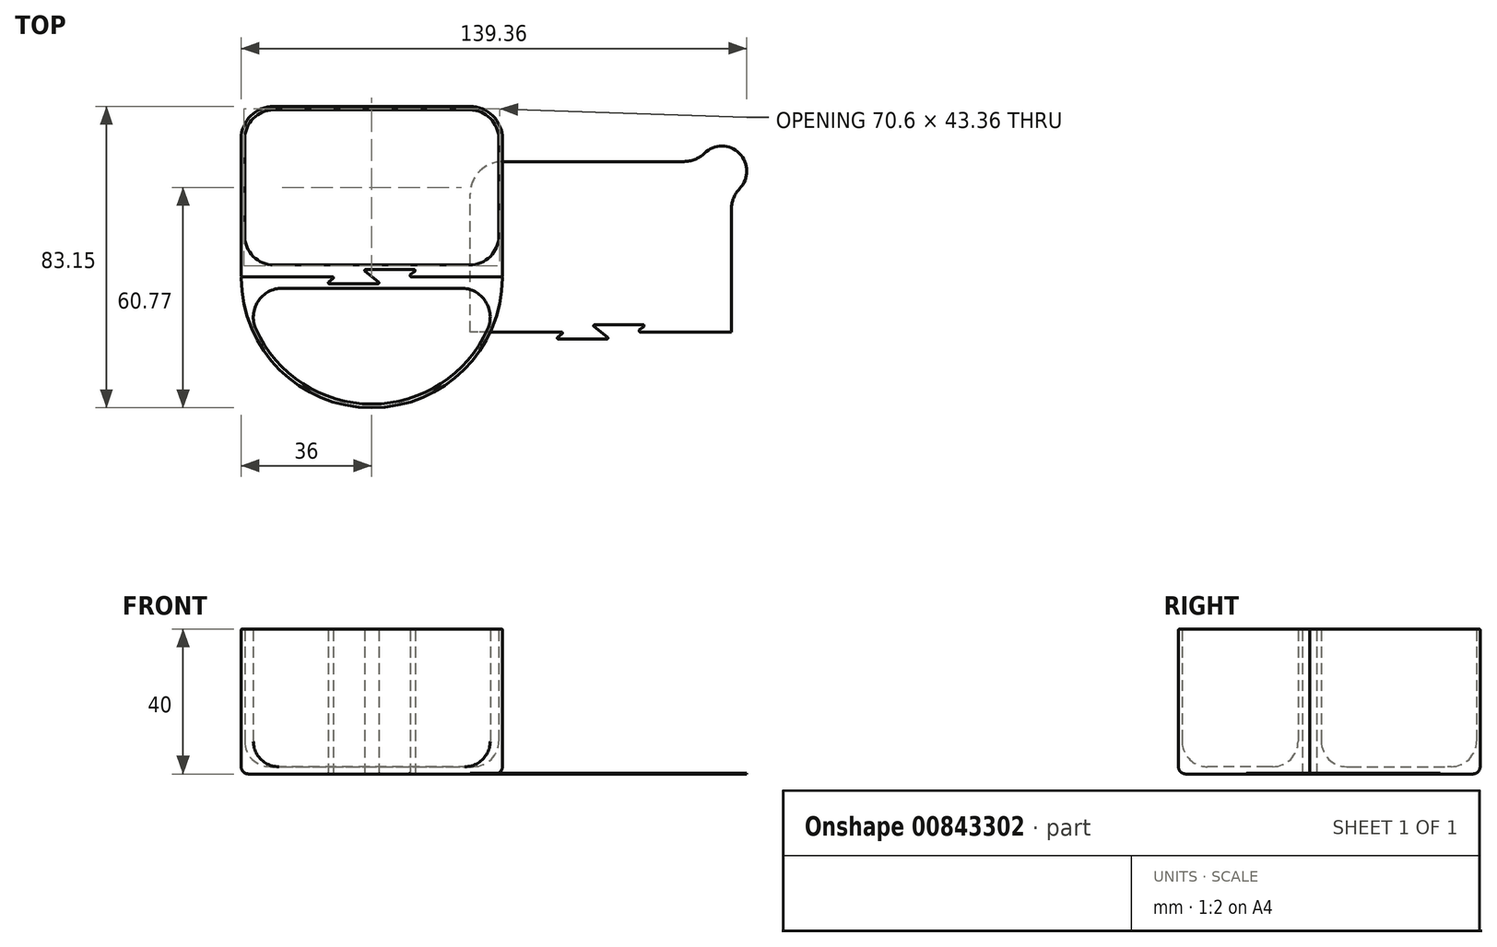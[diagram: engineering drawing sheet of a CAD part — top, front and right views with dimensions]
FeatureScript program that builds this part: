
annotation { "Feature Type Name" : "Feature", "Feature Type Description" : "" }
export const myFeature = defineFeature(function(context is Context, id is Id, definition is map)
    precondition{}
    {
        {
            var Q0;
            Q0=qCreatedBy(makeId("Top.planeOp"),FACE);
            var sketch = newSketch(context, id + "F0", { "sketchPlane" : qUnion([Q0])});
            skLineSegment(sketch, "E0.top", {"start": v(27, 22.5) * mm, "end": v(-27, 22.5) * mm});
            skLineSegment(sketch, "E0.left", {"start": v(35, -12.26) * mm, "end": v(35, 14.5) * mm});
            skLineSegment(sketch, "E0.right", {"start": v(-35, -12.26) * mm, "end": v(-35, 14.5) * mm});
            skPoint(sketch, "E0.middle", {"position": v(0, 0) * mm});
            skPoint(sketch, "E1.visualSharp", {"position": v(-35, 22.5) * mm});
            skArc(sketch, "E1.filletArc", {"start": v(-27, 22.5) * mm, "mid": v(-32.66, 20.16) * mm, "end": v(-35, 14.5) * mm});
            skPoint(sketch, "E2.visualSharp", {"position": v(35, 22.5) * mm});
            skArc(sketch, "E2.filletArc", {"start": v(35, 14.5) * mm, "mid": v(32.66, 20.16) * mm, "end": v(27, 22.5) * mm});
            skArc(sketch, "E3.0", {"start": v(36, 14.5) * mm, "mid": v(33.36, 20.86) * mm, "end": v(27, 23.5) * mm});
            skArc(sketch, "E3.1", {"start": v(-27, 23.5) * mm, "mid": v(-33.36, 20.86) * mm, "end": v(-36, 14.5) * mm});
            skLineSegment(sketch, "E3.2", {"start": v(-36, -23.5) * mm, "end": v(-36, 14.5) * mm});
            skLineSegment(sketch, "E3.3", {"start": v(27, 23.5) * mm, "end": v(-27, 23.5) * mm});
            skLineSegment(sketch, "E3.4", {"start": v(36, -23.5) * mm, "end": v(10.86, -23.5) * mm});
            skLineSegment(sketch, "E3.5", {"start": v(36, -23.5) * mm, "end": v(36, 14.5) * mm});
            skLineSegment(sketch, "E4", {"start": v(1.83, -24.97) * mm, "end": v(-1.83, -22.03) * mm});
            skLineSegment(sketch, "E5", {"start": v(1.64, -25.5) * mm, "end": v(-11.65, -25.5) * mm});
            skLineSegment(sketch, "E6", {"start": v(-11.83, -24.97) * mm, "end": v(-10.67, -24.03) * mm});
            skLineSegment(sketch, "E7", {"start": v(-1.64, -21.5) * mm, "end": v(11.64, -21.5) * mm});
            skLineSegment(sketch, "E8", {"start": v(11.83, -22.03) * mm, "end": v(10.67, -22.97) * mm});
            skLineSegment(sketch, "E9.trimOffspring", {"start": v(-10.86, -23.5) * mm, "end": v(-36, -23.5) * mm});
            skLineSegment(sketch, "E10", {"start": v(-27, -20.26) * mm, "end": v(27, -20.26) * mm});
            skPoint(sketch, "E11.visualSharp", {"position": v(-35, -20.26) * mm});
            skArc(sketch, "E11.filletArc", {"start": v(-35, -12.26) * mm, "mid": v(-32.66, -17.92) * mm, "end": v(-27, -20.26) * mm});
            skPoint(sketch, "E12.visualSharp", {"position": v(35, -20.26) * mm});
            skArc(sketch, "E12.filletArc", {"start": v(27, -20.26) * mm, "mid": v(32.66, -17.92) * mm, "end": v(35, -12.26) * mm});
            skPoint(sketch, "E13.visualSharp", {"position": v(-12.5, -25.5) * mm});
            skArc(sketch, "E13.filletArc", {"start": v(-11.83, -24.97) * mm, "mid": v(-11.93, -25.3) * mm, "end": v(-11.65, -25.5) * mm});
            skPoint(sketch, "E14.visualSharp", {"position": v(-10, -23.5) * mm});
            skArc(sketch, "E14.filletArc", {"start": v(-10.67, -24.03) * mm, "mid": v(-10.57, -23.7) * mm, "end": v(-10.86, -23.5) * mm});
            skPoint(sketch, "E15.visualSharp", {"position": v(2.5, -25.5) * mm});
            skArc(sketch, "E15.filletArc", {"start": v(1.64, -25.5) * mm, "mid": v(1.93, -25.3) * mm, "end": v(1.83, -24.97) * mm});
            skPoint(sketch, "E16.visualSharp", {"position": v(-2.5, -21.5) * mm});
            skArc(sketch, "E16.filletArc", {"start": v(-1.64, -21.5) * mm, "mid": v(-1.93, -21.7) * mm, "end": v(-1.83, -22.03) * mm});
            skPoint(sketch, "E17.visualSharp", {"position": v(12.5, -21.5) * mm});
            skArc(sketch, "E17.filletArc", {"start": v(11.83, -22.03) * mm, "mid": v(11.93, -21.7) * mm, "end": v(11.64, -21.5) * mm});
            skPoint(sketch, "E18.visualSharp", {"position": v(10, -23.5) * mm});
            skArc(sketch, "E18.filletArc", {"start": v(10.67, -22.97) * mm, "mid": v(10.57, -23.3) * mm, "end": v(10.86, -23.5) * mm});
            skSolve(sketch);
        }
        {
            var Q0;
            Q0=makeQuery(id+"F0.imprint","IMPRINT",FACE,{"disambiguationData":[TD([[makeQuery(id+"F0.imprint","IMPRINT",EDGE,{"derivedFrom":sQuery(id+"F0.wireOp",EDGE,"E0.top")}),-1.0]])]});
            extrude(context, id + "F1", {"entities" : qUnion([Q0]), "depth" : 40 * mm, "offsetDistance" : 25 * mm});
        }
        {
            var Q0;
            Q0=makeQuery(id+"F1.opExtrude","CAP_FACE",FACE,{"disambiguationData":[OSD([sQuery(id+"F0.wireOp",EDGE,"E0.top"),sQuery(id+"F0.wireOp",EDGE,"E0.left"),sQuery(id+"F0.wireOp",EDGE,"E0.right"),sQuery(id+"F0.wireOp",EDGE,"E1.filletArc"),sQuery(id+"F0.wireOp",EDGE,"E2.filletArc"),sQuery(id+"F0.wireOp",EDGE,"E3.0"),sQuery(id+"F0.wireOp",EDGE,"E3.1"),sQuery(id+"F0.wireOp",EDGE,"E3.2"),sQuery(id+"F0.wireOp",EDGE,"E3.3"),sQuery(id+"F0.wireOp",EDGE,"E3.4"),sQuery(id+"F0.wireOp",EDGE,"E3.5"),sQuery(id+"F0.wireOp",EDGE,"E4"),sQuery(id+"F0.wireOp",EDGE,"E5"),sQuery(id+"F0.wireOp",EDGE,"E6"),sQuery(id+"F0.wireOp",EDGE,"E7"),sQuery(id+"F0.wireOp",EDGE,"E8"),sQuery(id+"F0.wireOp",EDGE,"E9.trimOffspring"),sQuery(id+"F0.wireOp",EDGE,"E10"),sQuery(id+"F0.wireOp",EDGE,"E11.filletArc"),sQuery(id+"F0.wireOp",EDGE,"E12.filletArc")])],"isStart":true});
            var sketch = newSketch(context, id + "F2", { "sketchPlane" : qUnion([Q0])});
            skArc(sketch, "E19.0", {"start": v(-35, 12.26) * mm, "mid": v(-32.66, 17.92) * mm, "end": v(-27, 20.26) * mm});
            skLineSegment(sketch, "E19.1", {"start": v(-27, 20.26) * mm, "end": v(27, 20.26) * mm});
            skArc(sketch, "E19.2", {"start": v(27, 20.26) * mm, "mid": v(32.66, 17.92) * mm, "end": v(35, 12.26) * mm});
            skLineSegment(sketch, "E19.3", {"start": v(35, 12.26) * mm, "end": v(35, -14.5) * mm});
            skArc(sketch, "E19.4", {"start": v(35, -14.5) * mm, "mid": v(32.66, -20.16) * mm, "end": v(27, -22.5) * mm});
            skLineSegment(sketch, "E19.5", {"start": v(27, -22.5) * mm, "end": v(-27, -22.5) * mm});
            skArc(sketch, "E19.6", {"start": v(-27, -22.5) * mm, "mid": v(-32.66, -20.16) * mm, "end": v(-35, -14.5) * mm});
            skLineSegment(sketch, "E19.7", {"start": v(-35, 12.26) * mm, "end": v(-35, -14.5) * mm});
            skSolve(sketch);
        }
        {
            var Q0;
            Q0 = qSketchRegion(id + "F2", true);
            extrude(context, id + "F3", {"entities" : qUnion([Q0]), "operationType" : NewBodyOperationType.ADD, "oppositeDirection" : true, "depth" : 2 * mm, "offsetDistance" : 25 * mm});
        }
        {
            var Q0;
            Q0=makeQuery(id+"F1.opExtrude","CAP_EDGE",EDGE,{"disambiguationData":[OSD([sQuery(id+"F0.wireOp",EDGE,"E3.2")])],"isStart":true});
            var Q1;
            Q1=makeQuery(id+"F1.opExtrude","CAP_EDGE",EDGE,{"disambiguationData":[OSD([sQuery(id+"F0.wireOp",EDGE,"E3.1")])],"isStart":true});
            var Q2;
            Q2=makeQuery(id+"F1.opExtrude","CAP_EDGE",EDGE,{"disambiguationData":[OSD([sQuery(id+"F0.wireOp",EDGE,"E3.3")])],"isStart":true});
            var Q3;
            Q3=makeQuery(id+"F1.opExtrude","CAP_EDGE",EDGE,{"disambiguationData":[OSD([sQuery(id+"F0.wireOp",EDGE,"E3.0")])],"isStart":true});
            var Q4;
            Q4=makeQuery(id+"F1.opExtrude","CAP_EDGE",EDGE,{"disambiguationData":[OSD([sQuery(id+"F0.wireOp",EDGE,"E3.5")])],"isStart":true});
            fillet(context, id + "F4", {"entities" : qUnion([Q0, Q1, Q2, Q3, Q4]), "radius" : 2 * mm, "tangentPropagation" : true, "allowEdgeOverflow" : false});
        }
        {
            var Q0;
            Q0=makeQuery(id+"F3.opExtrude","CAP_FACE",FACE,{"disambiguationData":[OSD([sQuery(id+"F2.wireOp",EDGE,"E19.0"),sQuery(id+"F2.wireOp",EDGE,"E19.1"),sQuery(id+"F2.wireOp",EDGE,"E19.2"),sQuery(id+"F2.wireOp",EDGE,"E19.3"),sQuery(id+"F2.wireOp",EDGE,"E19.4"),sQuery(id+"F2.wireOp",EDGE,"E19.5"),sQuery(id+"F2.wireOp",EDGE,"E19.6"),sQuery(id+"F2.wireOp",EDGE,"E19.7")])],"isStart":false});
            fillet(context, id + "F5", {"entities" : qUnion([Q0]), "radius" : 7 * mm, "tangentPropagation" : true, "allowEdgeOverflow" : false});
        }
        {
            var Q0;
            Q0=makeQuery(id+"F1.opExtrude","CAP_FACE",FACE,{"disambiguationData":[OSD([sQuery(id+"F0.wireOp",EDGE,"E0.top"),sQuery(id+"F0.wireOp",EDGE,"E0.left"),sQuery(id+"F0.wireOp",EDGE,"E0.right"),sQuery(id+"F0.wireOp",EDGE,"E1.filletArc"),sQuery(id+"F0.wireOp",EDGE,"E2.filletArc"),sQuery(id+"F0.wireOp",EDGE,"E3.0"),sQuery(id+"F0.wireOp",EDGE,"E3.1"),sQuery(id+"F0.wireOp",EDGE,"E3.2"),sQuery(id+"F0.wireOp",EDGE,"E3.3"),sQuery(id+"F0.wireOp",EDGE,"E3.4"),sQuery(id+"F0.wireOp",EDGE,"E3.5"),sQuery(id+"F0.wireOp",EDGE,"E4"),sQuery(id+"F0.wireOp",EDGE,"E5"),sQuery(id+"F0.wireOp",EDGE,"E6"),sQuery(id+"F0.wireOp",EDGE,"E7"),sQuery(id+"F0.wireOp",EDGE,"E8"),sQuery(id+"F0.wireOp",EDGE,"E9.trimOffspring"),sQuery(id+"F0.wireOp",EDGE,"E10"),sQuery(id+"F0.wireOp",EDGE,"E11.filletArc"),sQuery(id+"F0.wireOp",EDGE,"E12.filletArc")])],"isStart":false});
            var Q1;
            Q1=makeQuery(id+"F3.boolean.opBoolean","MERGE",FACE,{"derivedFrom":[makeQuery(id+"F1.opExtrude","CAP_FACE",FACE,{"disambiguationData":[OSD([sQuery(id+"F0.wireOp",EDGE,"E0.top"),sQuery(id+"F0.wireOp",EDGE,"E0.left"),sQuery(id+"F0.wireOp",EDGE,"E0.right"),sQuery(id+"F0.wireOp",EDGE,"E1.filletArc"),sQuery(id+"F0.wireOp",EDGE,"E2.filletArc"),sQuery(id+"F0.wireOp",EDGE,"E3.0"),sQuery(id+"F0.wireOp",EDGE,"E3.1"),sQuery(id+"F0.wireOp",EDGE,"E3.2"),sQuery(id+"F0.wireOp",EDGE,"E3.3"),sQuery(id+"F0.wireOp",EDGE,"E3.4"),sQuery(id+"F0.wireOp",EDGE,"E3.5"),sQuery(id+"F0.wireOp",EDGE,"E4"),sQuery(id+"F0.wireOp",EDGE,"E5"),sQuery(id+"F0.wireOp",EDGE,"E6"),sQuery(id+"F0.wireOp",EDGE,"E7"),sQuery(id+"F0.wireOp",EDGE,"E8"),sQuery(id+"F0.wireOp",EDGE,"E9.trimOffspring"),sQuery(id+"F0.wireOp",EDGE,"E10"),sQuery(id+"F0.wireOp",EDGE,"E11.filletArc"),sQuery(id+"F0.wireOp",EDGE,"E12.filletArc")])],"isStart":true}),makeQuery(id+"F3.opExtrude","CAP_FACE",FACE,{"disambiguationData":[OSD([sQuery(id+"F2.wireOp",EDGE,"E19.0"),sQuery(id+"F2.wireOp",EDGE,"E19.1"),sQuery(id+"F2.wireOp",EDGE,"E19.2"),sQuery(id+"F2.wireOp",EDGE,"E19.3"),sQuery(id+"F2.wireOp",EDGE,"E19.4"),sQuery(id+"F2.wireOp",EDGE,"E19.5"),sQuery(id+"F2.wireOp",EDGE,"E19.6"),sQuery(id+"F2.wireOp",EDGE,"E19.7")])],"isStart":true})]});
            fillet(context, id + "F6", {"entities" : qUnion([Q0, Q1]), "radius" : 0.3 * mm, "tangentPropagation" : true, "allowEdgeOverflow" : false});
        }
        {
            var Q0;
            Q0=makeQuery(id+"F1.opExtrude","SWEPT_BODY",BODY,{"disambiguationData":[OSD([sQuery(id+"F0.wireOp",EDGE,"E0.top"),sQuery(id+"F0.wireOp",EDGE,"E0.left"),sQuery(id+"F0.wireOp",EDGE,"E0.right"),sQuery(id+"F0.wireOp",EDGE,"E1.filletArc"),sQuery(id+"F0.wireOp",EDGE,"E2.filletArc"),sQuery(id+"F0.wireOp",EDGE,"E3.0"),sQuery(id+"F0.wireOp",EDGE,"E3.1"),sQuery(id+"F0.wireOp",EDGE,"E3.2"),sQuery(id+"F0.wireOp",EDGE,"E3.3"),sQuery(id+"F0.wireOp",EDGE,"E3.4"),sQuery(id+"F0.wireOp",EDGE,"E3.5"),sQuery(id+"F0.wireOp",EDGE,"E4"),sQuery(id+"F0.wireOp",EDGE,"E5"),sQuery(id+"F0.wireOp",EDGE,"E6"),sQuery(id+"F0.wireOp",EDGE,"E7"),sQuery(id+"F0.wireOp",EDGE,"E8"),sQuery(id+"F0.wireOp",EDGE,"E9.trimOffspring"),sQuery(id+"F0.wireOp",EDGE,"E10"),sQuery(id+"F0.wireOp",EDGE,"E11.filletArc"),sQuery(id+"F0.wireOp",EDGE,"E12.filletArc"),sQuery(id+"F0.wireOp",EDGE,"E13.filletArc"),sQuery(id+"F0.wireOp",EDGE,"E14.filletArc"),sQuery(id+"F0.wireOp",EDGE,"E15.filletArc"),sQuery(id+"F0.wireOp",EDGE,"E16.filletArc"),sQuery(id+"F0.wireOp",EDGE,"E17.filletArc"),sQuery(id+"F0.wireOp",EDGE,"E18.filletArc")])]});
            transform(context, id + "F7", {"entities" : qUnion([Q0]), "transformType" : TransformType.TRANSLATION_3D, "dx" : 0 * mm, "dy" : 0 * mm, "dz" : 0 * mm, "makeCopy" : true});
        }
        {
            var Q0;
            Q0=qCreatedBy(makeId("Top.planeOp"),FACE);
            var Q1;
            Q1=qCreatedBy(makeId("Top.planeOp"),FACE);
            var Q2;
            Q2=qCreatedBy(makeId("Top.planeOp"),FACE);
            var Q3;
            Q3=qCreatedBy(makeId("Top.planeOp"),FACE);
            var Q4;
            Q4=qCreatedBy(makeId("Top.planeOp"),FACE);
            var Q5;
            Q5=qCreatedBy(makeId("Top.planeOp"),FACE);
            var sketch = newSketch(context, id + "F8", { "sketchPlane" : qUnion([Q0, Q1, Q2, Q3, Q4, Q5])});
            skPoint(sketch, "E20.3", {"position": v(0, 0) * mm});
            skPoint(sketch, "E20.4", {"position": v(-35, 22.5) * mm});
            skPoint(sketch, "E20.6", {"position": v(35, 22.5) * mm});
            skLineSegment(sketch, "E20.12", {"start": v(36, -23.5) * mm, "end": v(10.86, -23.5) * mm});
            skLineSegment(sketch, "E20.14", {"start": v(1.83, -24.97) * mm, "end": v(-1.83, -22.03) * mm});
            skLineSegment(sketch, "E20.15", {"start": v(1.64, -25.5) * mm, "end": v(-11.65, -25.5) * mm});
            skLineSegment(sketch, "E20.16", {"start": v(-11.83, -24.97) * mm, "end": v(-10.67, -24.03) * mm});
            skLineSegment(sketch, "E20.17", {"start": v(-1.64, -21.5) * mm, "end": v(11.64, -21.5) * mm});
            skLineSegment(sketch, "E20.18", {"start": v(11.83, -22.03) * mm, "end": v(10.67, -22.97) * mm});
            skLineSegment(sketch, "E20.19", {"start": v(-10.86, -23.5) * mm, "end": v(-36, -23.5) * mm});
            skPoint(sketch, "E20.21", {"position": v(-35, -20.26) * mm});
            skPoint(sketch, "E20.23", {"position": v(35, -20.26) * mm});
            skPoint(sketch, "E20.25", {"position": v(-12.5, -25.5) * mm});
            skArc(sketch, "E20.26", {"start": v(-11.83, -24.97) * mm, "mid": v(-11.93, -25.3) * mm, "end": v(-11.65, -25.5) * mm});
            skPoint(sketch, "E20.27", {"position": v(-10, -23.5) * mm});
            skArc(sketch, "E20.28", {"start": v(-10.67, -24.03) * mm, "mid": v(-10.57, -23.7) * mm, "end": v(-10.86, -23.5) * mm});
            skPoint(sketch, "E20.29", {"position": v(2.5, -25.5) * mm});
            skArc(sketch, "E20.30", {"start": v(1.64, -25.5) * mm, "mid": v(1.93, -25.3) * mm, "end": v(1.83, -24.97) * mm});
            skPoint(sketch, "E20.31", {"position": v(-2.5, -21.5) * mm});
            skArc(sketch, "E20.32", {"start": v(-1.64, -21.5) * mm, "mid": v(-1.93, -21.7) * mm, "end": v(-1.83, -22.03) * mm});
            skPoint(sketch, "E20.33", {"position": v(12.5, -21.5) * mm});
            skArc(sketch, "E20.34", {"start": v(11.83, -22.03) * mm, "mid": v(11.93, -21.7) * mm, "end": v(11.64, -21.5) * mm});
            skPoint(sketch, "E20.35", {"position": v(10, -23.5) * mm});
            skArc(sketch, "E20.36", {"start": v(10.67, -22.97) * mm, "mid": v(10.57, -23.3) * mm, "end": v(10.86, -23.5) * mm});
            skArc(sketch, "E21", {"start": v(-36, -23.5) * mm, "mid": v(0, -59.65) * mm, "end": v(36, -23.5) * mm});
            skArc(sketch, "E22.0", {"start": v(-31.95, -37.93) * mm, "mid": v(0, -58.65) * mm, "end": v(31.95, -37.93) * mm});
            skLineSegment(sketch, "E23", {"start": v(-24.65, -26.66) * mm, "end": v(24.65, -26.66) * mm});
            skPoint(sketch, "E24.visualSharp", {"position": v(34.87, -26.66) * mm});
            skArc(sketch, "E24.filletArc", {"start": v(31.95, -37.93) * mm, "mid": v(31.36, -30.3) * mm, "end": v(24.65, -26.66) * mm});
            skPoint(sketch, "E25.visualSharp", {"position": v(-34.87, -26.66) * mm});
            skArc(sketch, "E25.filletArc", {"start": v(-24.65, -26.66) * mm, "mid": v(-31.36, -30.3) * mm, "end": v(-31.95, -37.93) * mm});
            skSolve(sketch);
        }
        {
            var Q0;
            Q0 = qSketchRegion(id + "F8", true);
            extrude(context, id + "F9", {"entities" : qUnion([Q0]), "depth" : 40 * mm, "offsetDistance" : 25 * mm});
        }
        {
            var Q0;
            Q0=qCreatedBy(makeId("Top.planeOp"),FACE);
            var Q1;
            Q1=makeQuery(id+"F8.imprint","IMPRINT",FACE,{"disambiguationData":[TD([[makeQuery(id+"F8.imprint","IMPRINT",EDGE,{"derivedFrom":sQuery(id+"F8.wireOp",EDGE,"E22.0")}),1.0]])]});
            var sketch = newSketch(context, id + "F10", { "sketchPlane" : qUnion([Q0, Q1])});
            skSolve(sketch);
        }
        {
            var Q0;
            Q0 = qSketchRegion(id + "F10", true);
            var Q1;
            Q1=makeQuery(id+"F8.imprint","IMPRINT",FACE,{"disambiguationData":[TD([[makeQuery(id+"F8.imprint","IMPRINT",EDGE,{"derivedFrom":sQuery(id+"F8.wireOp",EDGE,"E22.0")}),1.0]])]});
            extrude(context, id + "F11", {"entities" : qUnion([Q0, Q1]), "operationType" : NewBodyOperationType.ADD, "depth" : 2 * mm, "offsetDistance" : 25 * mm});
        }
        {
            var Q0;
            Q0=makeQuery(id+"F11.opExtrude","CAP_FACE",FACE,{"disambiguationData":[OSD([sQuery(id+"F8.wireOp",EDGE,"E22.0"),sQuery(id+"F8.wireOp",EDGE,"E23"),sQuery(id+"F8.wireOp",EDGE,"E24.filletArc"),sQuery(id+"F8.wireOp",EDGE,"E25.filletArc")])],"isStart":false});
            fillet(context, id + "F12", {"entities" : qUnion([Q0]), "radius" : 7 * mm, "tangentPropagation" : true, "allowEdgeOverflow" : false});
        }
        {
            var Q0;
            Q0=makeQuery(id+"F9.opExtrude","CAP_FACE",FACE,{"disambiguationData":[OSD([sQuery(id+"F8.wireOp",EDGE,"E20.12"),sQuery(id+"F8.wireOp",EDGE,"E20.14"),sQuery(id+"F8.wireOp",EDGE,"E20.15"),sQuery(id+"F8.wireOp",EDGE,"E20.16"),sQuery(id+"F8.wireOp",EDGE,"E20.17"),sQuery(id+"F8.wireOp",EDGE,"E20.18"),sQuery(id+"F8.wireOp",EDGE,"E20.19"),sQuery(id+"F8.wireOp",EDGE,"E20.26"),sQuery(id+"F8.wireOp",EDGE,"E20.28"),sQuery(id+"F8.wireOp",EDGE,"E20.30"),sQuery(id+"F8.wireOp",EDGE,"E20.32"),sQuery(id+"F8.wireOp",EDGE,"E20.34"),sQuery(id+"F8.wireOp",EDGE,"E20.36"),sQuery(id+"F8.wireOp",EDGE,"E21"),sQuery(id+"F8.wireOp",EDGE,"E22.0"),sQuery(id+"F8.wireOp",EDGE,"E23"),sQuery(id+"F8.wireOp",EDGE,"E24.filletArc"),sQuery(id+"F8.wireOp",EDGE,"E25.filletArc")])],"isStart":false});
            fillet(context, id + "F13", {"entities" : qUnion([Q0]), "radius" : 0.3 * mm, "tangentPropagation" : true, "allowEdgeOverflow" : false});
        }
        {
            var Q0;
            Q0=makeQuery(id+"F9.opExtrude","CAP_EDGE",EDGE,{"disambiguationData":[OSD([sQuery(id+"F8.wireOp",EDGE,"E21")])],"isStart":true});
            fillet(context, id + "F14", {"entities" : qUnion([Q0]), "radius" : 2 * mm, "tangentPropagation" : true, "allowEdgeOverflow" : false});
        }
        {
            var Q0;
            {var subQ0=sQuery(id+"F8.wireOp",EDGE,"E25.filletArc");var subQ1=sQuery(id+"F8.wireOp",EDGE,"E24.filletArc");var subQ2=sQuery(id+"F8.wireOp",EDGE,"E23");var subQ3=sQuery(id+"F8.wireOp",EDGE,"E22.0");Q0=makeQuery(id+"F11.boolean.opBoolean","MERGE",FACE,{"derivedFrom":[makeQuery(id+"F9.opExtrude","CAP_FACE",FACE,{"disambiguationData":[OSD([sQuery(id+"F8.wireOp",EDGE,"E20.12"),sQuery(id+"F8.wireOp",EDGE,"E20.14"),sQuery(id+"F8.wireOp",EDGE,"E20.15"),sQuery(id+"F8.wireOp",EDGE,"E20.16"),sQuery(id+"F8.wireOp",EDGE,"E20.17"),sQuery(id+"F8.wireOp",EDGE,"E20.18"),sQuery(id+"F8.wireOp",EDGE,"E20.19"),sQuery(id+"F8.wireOp",EDGE,"E20.26"),sQuery(id+"F8.wireOp",EDGE,"E20.28"),sQuery(id+"F8.wireOp",EDGE,"E20.30"),sQuery(id+"F8.wireOp",EDGE,"E20.32"),sQuery(id+"F8.wireOp",EDGE,"E20.34"),sQuery(id+"F8.wireOp",EDGE,"E20.36"),sQuery(id+"F8.wireOp",EDGE,"E21"),subQ3,subQ2,subQ1,subQ0])],"isStart":true}),makeQuery(id+"F11.opExtrude","CAP_FACE",FACE,{"disambiguationData":[OSD([subQ3,subQ2,subQ1,subQ0])],"isStart":true})]});}
            fillet(context, id + "F15", {"entities" : qUnion([Q0]), "radius" : 0.3 * mm, "tangentPropagation" : true, "allowEdgeOverflow" : false});
        }
        {
            var Q0;
            Q0=qCreatedBy(makeId("Top.planeOp"),FACE);
            var Q1;
            Q1=makeQuery(id+"F1.opExtrude","CAP_FACE",FACE,{"disambiguationData":[OSD([sQuery(id+"F0.wireOp",EDGE,"E0.top"),sQuery(id+"F0.wireOp",EDGE,"E0.left"),sQuery(id+"F0.wireOp",EDGE,"E0.right"),sQuery(id+"F0.wireOp",EDGE,"E1.filletArc"),sQuery(id+"F0.wireOp",EDGE,"E2.filletArc"),sQuery(id+"F0.wireOp",EDGE,"E3.0"),sQuery(id+"F0.wireOp",EDGE,"E3.1"),sQuery(id+"F0.wireOp",EDGE,"E3.2"),sQuery(id+"F0.wireOp",EDGE,"E3.3"),sQuery(id+"F0.wireOp",EDGE,"E3.4"),sQuery(id+"F0.wireOp",EDGE,"E3.5"),sQuery(id+"F0.wireOp",EDGE,"E4"),sQuery(id+"F0.wireOp",EDGE,"E5"),sQuery(id+"F0.wireOp",EDGE,"E6"),sQuery(id+"F0.wireOp",EDGE,"E7"),sQuery(id+"F0.wireOp",EDGE,"E8"),sQuery(id+"F0.wireOp",EDGE,"E9.trimOffspring"),sQuery(id+"F0.wireOp",EDGE,"E10"),sQuery(id+"F0.wireOp",EDGE,"E11.filletArc"),sQuery(id+"F0.wireOp",EDGE,"E12.filletArc"),sQuery(id+"F0.wireOp",EDGE,"E13.filletArc"),sQuery(id+"F0.wireOp",EDGE,"E14.filletArc"),sQuery(id+"F0.wireOp",EDGE,"E15.filletArc"),sQuery(id+"F0.wireOp",EDGE,"E16.filletArc"),sQuery(id+"F0.wireOp",EDGE,"E17.filletArc"),sQuery(id+"F0.wireOp",EDGE,"E18.filletArc")])],"isStart":false});
            var Q2;
            Q2=qCreatedBy(makeId("Top.planeOp"),FACE);
            var sketch = newSketch(context, id + "F16", { "sketchPlane" : qUnion([Q0, Q1, Q2])});
            skArc(sketch, "E26.1", {"start": v(36.11, 8.26) * mm, "mid": v(29.75, 5.62) * mm, "end": v(27.11, -0.74) * mm});
            skLineSegment(sketch, "E26.2", {"start": v(27.11, -38.74) * mm, "end": v(27.11, -0.74) * mm});
            skLineSegment(sketch, "E26.3", {"start": v(86.06, 8.26) * mm, "end": v(36.11, 8.26) * mm});
            skLineSegment(sketch, "E26.4", {"start": v(99.11, -38.74) * mm, "end": v(73.97, -38.74) * mm});
            skLineSegment(sketch, "E26.5", {"start": v(99.11, -38.74) * mm, "end": v(99.11, -4.8) * mm});
            skLineSegment(sketch, "E27", {"start": v(64.94, -40.2) * mm, "end": v(61.28, -37.28) * mm});
            skLineSegment(sketch, "E28", {"start": v(64.76, -40.74) * mm, "end": v(51.47, -40.74) * mm});
            skLineSegment(sketch, "E29", {"start": v(51.28, -40.2) * mm, "end": v(52.44, -39.28) * mm});
            skLineSegment(sketch, "E30", {"start": v(61.47, -36.74) * mm, "end": v(74.76, -36.74) * mm});
            skLineSegment(sketch, "E31", {"start": v(74.94, -37.28) * mm, "end": v(73.78, -38.2) * mm});
            skLineSegment(sketch, "E32.trimOffspring", {"start": v(52.26, -38.74) * mm, "end": v(27.11, -38.74) * mm});
            skArc(sketch, "E33.filletArc", {"start": v(51.28, -40.2) * mm, "mid": v(51.18, -40.54) * mm, "end": v(51.47, -40.74) * mm});
            skArc(sketch, "E34.filletArc", {"start": v(52.44, -39.28) * mm, "mid": v(52.54, -38.94) * mm, "end": v(52.26, -38.74) * mm});
            skArc(sketch, "E35.filletArc", {"start": v(64.76, -40.74) * mm, "mid": v(65.04, -40.54) * mm, "end": v(64.94, -40.2) * mm});
            skArc(sketch, "E36.filletArc", {"start": v(61.47, -36.74) * mm, "mid": v(61.18, -36.94) * mm, "end": v(61.28, -37.28) * mm});
            skArc(sketch, "E37.filletArc", {"start": v(74.94, -37.28) * mm, "mid": v(75.04, -36.94) * mm, "end": v(74.76, -36.74) * mm});
            skArc(sketch, "E38.filletArc", {"start": v(73.78, -38.2) * mm, "mid": v(73.68, -38.54) * mm, "end": v(73.97, -38.74) * mm});
            skArc(sketch, "E39", {"start": v(101.4, 0.8) * mm, "mid": v(101.35, 10.5) * mm, "end": v(91.66, 10.54) * mm});
            skPoint(sketch, "E40.visualSharp", {"position": v(90.11, 8.26) * mm});
            skArc(sketch, "E40.filletArc", {"start": v(86.06, 8.26) * mm, "mid": v(89.08, 8.85) * mm, "end": v(91.66, 10.54) * mm});
            skPoint(sketch, "E41.visualSharp", {"position": v(99.11, -0.74) * mm});
            skArc(sketch, "E41.filletArc", {"start": v(101.4, 0.8) * mm, "mid": v(99.7, -1.77) * mm, "end": v(99.11, -4.8) * mm});
            skSolve(sketch);
        }
        {
            var Q0;
            Q0=makeQuery(id+"F16.imprint","IMPRINT",FACE,{"disambiguationData":[TD([[makeQuery(id+"F16.imprint","IMPRINT",EDGE,{"derivedFrom":sQuery(id+"F16.wireOp",EDGE,"E26.1")}),1.0]])]});
            extrude(context, id + "F17", {"entities" : qUnion([Q0]), "depth" : 0.2 * mm, "offsetDistance" : 25 * mm});
        }
    });
